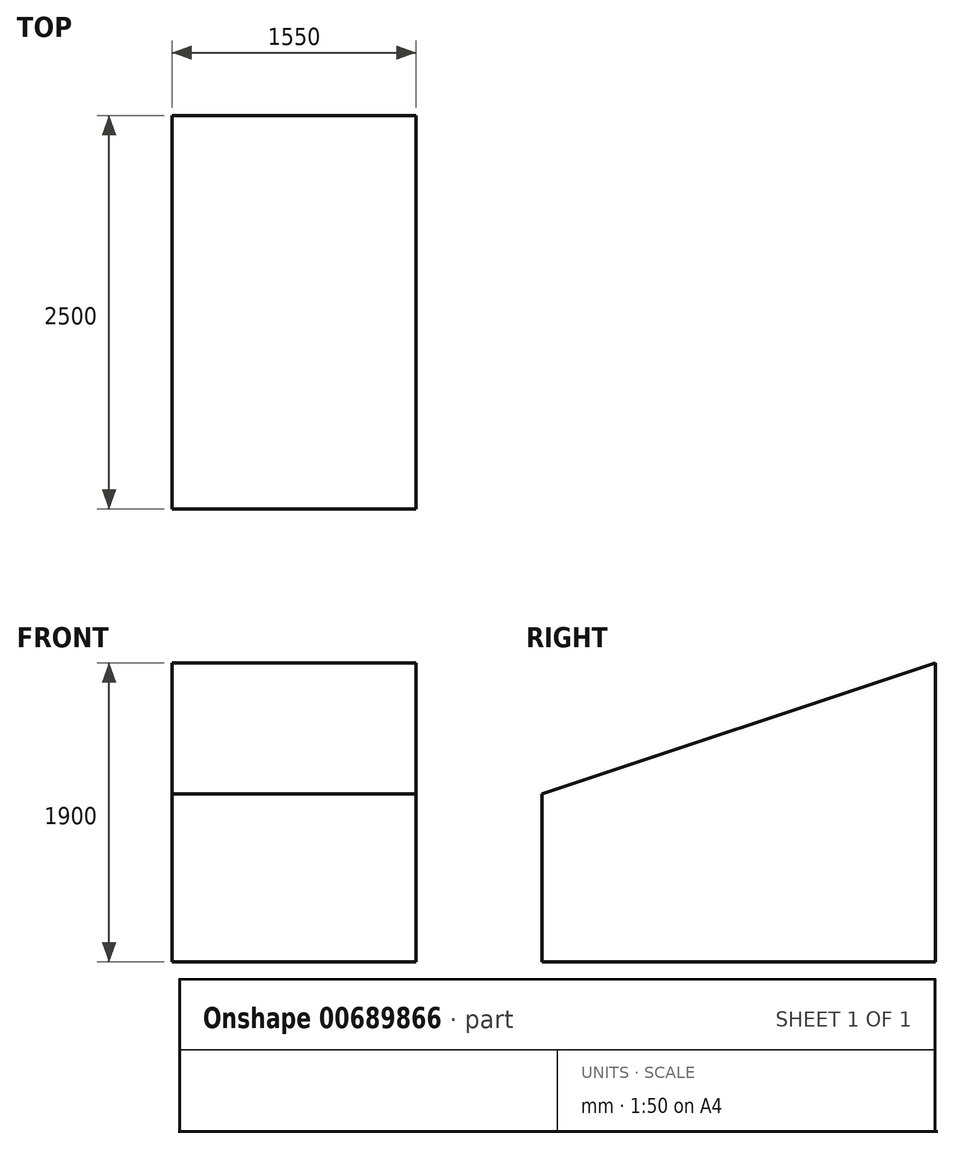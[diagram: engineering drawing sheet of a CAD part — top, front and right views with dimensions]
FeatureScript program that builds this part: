
annotation { "Feature Type Name" : "Feature", "Feature Type Description" : "" }
export const myFeature = defineFeature(function(context is Context, id is Id, definition is map)
    precondition{}
    {
        {
            var Q0;
            Q0=qCreatedBy(makeId("Top.planeOp"),FACE);
            var sketch = newSketch(context, id + "F0", { "sketchPlane" : qUnion([Q0])});
            skLineSegment(sketch, "E0.bottom", {"start": v(-775, 1250) * mm, "end": v(775, 1250) * mm});
            skLineSegment(sketch, "E0.top", {"start": v(-775, -1250) * mm, "end": v(775, -1250) * mm});
            skLineSegment(sketch, "E0.left", {"start": v(-775, 1250) * mm, "end": v(-775, -1250) * mm});
            skLineSegment(sketch, "E0.right", {"start": v(775, 1250) * mm, "end": v(775, -1250) * mm});
            skPoint(sketch, "E0.middle", {"position": v(0, 0) * mm});
            skSolve(sketch);
        }
        {
            var Q0;
            Q0 = qSketchRegion(id + "F0", true);
            extrude(context, id + "F1", {"entities" : qUnion([Q0]), "depth" : 1900 * mm, "offsetDistance" : 25.4 * mm});
        }
        {
            var Q0;
            Q0=makeQuery(id+"F1.opExtrude","SWEPT_FACE",FACE,{"disambiguationData":[OSD([sQuery(id+"F0.wireOp",EDGE,"E0.right")])]});
            var sketch = newSketch(context, id + "F2", { "sketchPlane" : qUnion([Q0])});
            skLineSegment(sketch, "E1", {"start": v(1250, 1900) * mm, "end": v(-1250, 1066.8) * mm});
            skLineSegment(sketch, "E2", {"start": v(-1250, 1066.8) * mm, "end": v(-1250, 1900) * mm});
            skLineSegment(sketch, "E3", {"start": v(-1250, 1900) * mm, "end": v(1250, 1900) * mm});
            skSolve(sketch);
        }
        {
            var Q0;
            Q0 = qSketchRegion(id + "F2", true);
            extrude(context, id + "F3", {"entities" : qUnion([Q0]), "operationType" : NewBodyOperationType.REMOVE, "endBound" : BoundingType.THROUGH_ALL, "oppositeDirection" : true, "depth" : 25.4 * mm, "offsetDistance" : 25.4 * mm});
        }
    });
